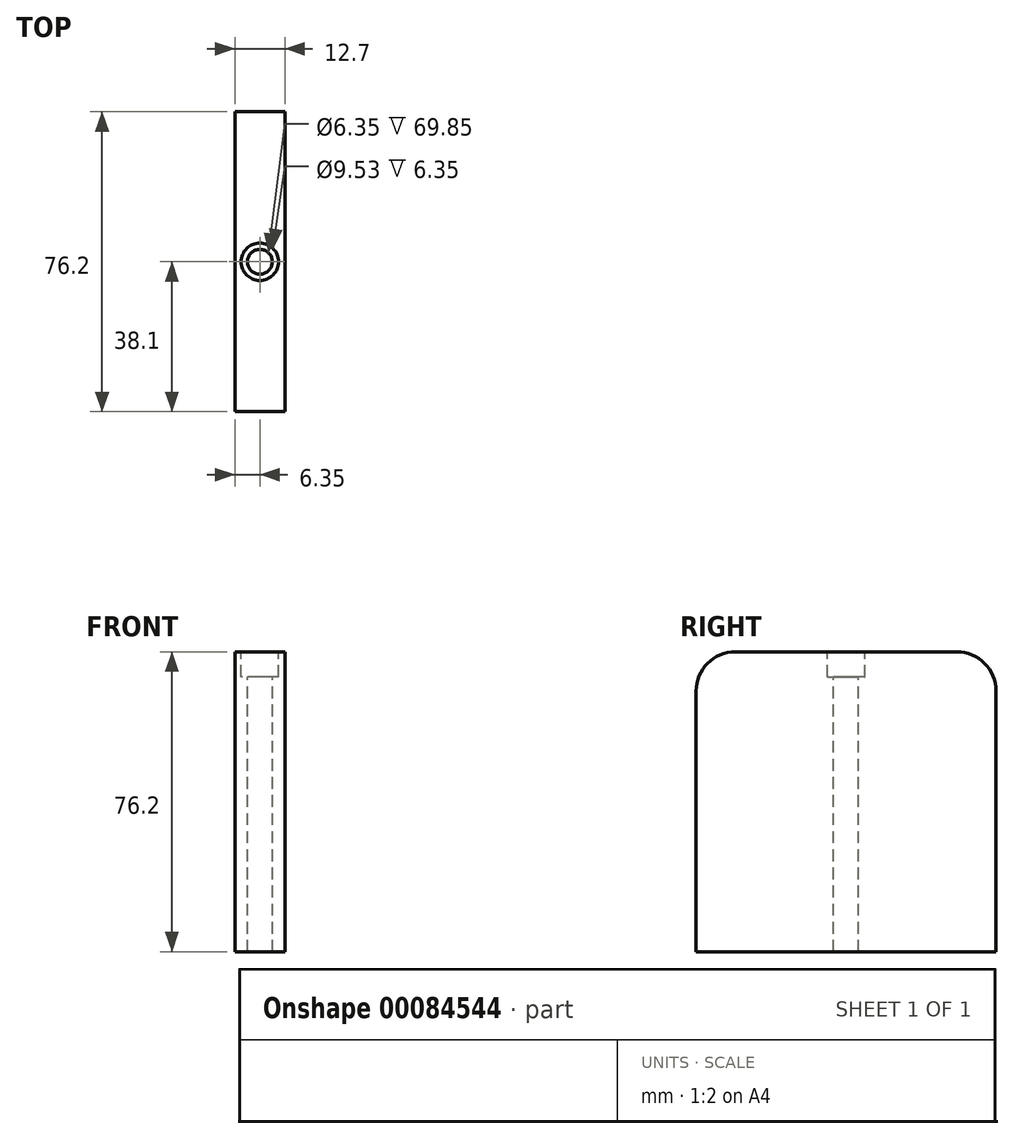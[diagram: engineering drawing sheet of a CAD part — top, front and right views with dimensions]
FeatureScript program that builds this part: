
annotation { "Feature Type Name" : "Feature", "Feature Type Description" : "" }
export const myFeature = defineFeature(function(context is Context, id is Id, definition is map)
    precondition{}
    {
        {
            var Q0;
            Q0=qCreatedBy(makeId("Front.planeOp"),FACE);
            var sketch = newSketch(context, id + "F0", { "sketchPlane" : qUnion([Q0]) });
            skLineSegment(sketch, "E0.bottom", {"start": v(-6.35, 38.1) * mm, "end": v(6.35, 38.1) * mm});
            skLineSegment(sketch, "E0.top", {"start": v(-6.35, -38.1) * mm, "end": v(6.35, -38.1) * mm});
            skLineSegment(sketch, "E0.left", {"start": v(-6.35, 38.1) * mm, "end": v(-6.35, -38.1) * mm});
            skLineSegment(sketch, "E0.right", {"start": v(6.35, 38.1) * mm, "end": v(6.35, -38.1) * mm});
            skPoint(sketch, "E0.middle", {"position": v(0, 0) * mm});
            skSolve(sketch);
        }
        {
            var Q0;
            Q0 = qSketchRegion(id + "F0", true);
            extrude(context, id + "F1", {"entities" : qUnion([Q0]), "depth" : 76.2 * mm});
        }
        {
            var Q0;
            Q0=makeQuery(id+"F1.opExtrude","SWEPT_FACE",FACE,{"disambiguationData":[OSD([sQuery(id+"F0.wireOp",EDGE,"E0.bottom")])]});
            var sketch = newSketch(context, id + "F2", { "sketchPlane" : qUnion([Q0]) });
            skPoint(sketch, "E1", {"position": v(0, -38.1) * mm});
            skPoint(sketch, "E1.positionSnap0", {"position": v(6.35, -38.1) * mm});
            skSolve(sketch);
        }
        {
            var Q0;
            Q0=sQuery(id+"F2.wireOp",VERTEX,"E1");
            var Q1;
            Q1=makeQuery(id+"F1.opExtrude","SWEPT_BODY",BODY,{"disambiguationData":[OSD([sQuery(id+"F0.wireOp",EDGE,"E0.bottom"),sQuery(id+"F0.wireOp",EDGE,"E0.top"),sQuery(id+"F0.wireOp",EDGE,"E0.left"),sQuery(id+"F0.wireOp",EDGE,"E0.right")])]});
            hole(context, id + "F3", {"style" : HoleStyle.C_BORE, "endStyle" : HoleEndStyle.THROUGH, "holeDiameter" : 6.35 * mm, "cBoreDiameter" : 9.52 * mm, "cBoreDepth" : 6.35 * mm, "tappedDepth" : 12 * mm, "tapClearance" : 3, "locations" : qUnion([Q0]), "scope" : qUnion([Q1])});
        }
        {
            var Q0;
            Q0=makeQuery(id+"F1.opExtrude","CAP_EDGE",EDGE,{"disambiguationData":[OSD([sQuery(id+"F0.wireOp",EDGE,"E0.bottom")])],"isStart":false});
            var Q1;
            Q1=makeQuery(id+"F1.opExtrude","CAP_EDGE",EDGE,{"disambiguationData":[OSD([sQuery(id+"F0.wireOp",EDGE,"E0.bottom")])],"isStart":true});
            fillet(context, id + "F4", {"entities" : qUnion([Q0, Q1]), "radius" : 10 * mm, "tangentPropagation" : true, "conicFillet" : false});
        }
    });
